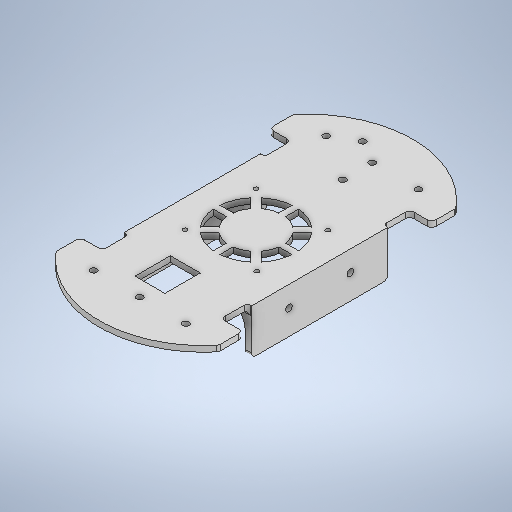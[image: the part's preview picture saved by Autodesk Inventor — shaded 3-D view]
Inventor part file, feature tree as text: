
AUTODESK INVENTOR PART (.ipt)
format: ipt  version: 2025.2 (Build 292293000, 293)  size: 749,056 bytes
history: native  units: mm
features: fillet x34, extrude x14, sketch x14
ambient origin geometry x8: Origin, YZ Plane, XZ Plane, XY Plane, X Axis, Y Axis, Z Axis, Center Point
bodies: Solid1 (feature_tree)
feature tree (62):
  extrude  "Extrusion1"  Depth=11.0mm
  fillet  "Face Fillet1"
  fillet  "Face Fillet2"
  fillet  "Face Fillet3"
  fillet  "Face Fillet4"
  fillet  "Face Fillet5"
  fillet  "Face Fillet6"
  fillet  "Face Fillet7"
  fillet  "Face Fillet8"
  fillet  "Face Fillet9"
  fillet  "Face Fillet10"
  fillet  "Face Fillet11"
  fillet  "Face Fillet12"
  extrude  "Extrusion3"  Depth=17.5mm
  sketch  "Sketch8"  dims[d23=2.0mm d24=2.0mm]
  sketch  "Sketch9"  dims[d25=2.0mm d26=2.0mm]
  extrude  "Extrusion4"  Depth=74.0mm
  sketch  "Sketch5"  dims[d16=27.0mm d17=2.6mm d18=0.0mm]
  sketch  "Sketch6"  dims[d19=2.0mm d20=2.0mm]
  sketch  "Sketch7"  dims[d21=2.0mm d22=2.0mm]
  extrude  "Extrusion11"  Depth=27.0mm
  extrude  "Extrusion12"  Depth=2.6mm TaperAngle=0.0deg
  extrude  "Extrusion13"  Depth=2.0mm
  extrude  "Extrusion14"  Depth=2.0mm
  extrude  "Extrusion15"  Depth=2.0mm
  fillet  "Face Fillet17"
  fillet  "Face Fillet18"
  fillet  "Face Fillet19"
  fillet  "Face Fillet20"
  extrude  "Extrusion16"  Depth=2.0mm
  sketch  "Sketch15"  dims[d27=2.0mm d39=0.0mm d40=40.0mm]
  extrude  "Extrusion17"  Depth=40.0mm TaperAngle=0.0deg
  sketch  "Sketch17"  dims[d48=2.0mm d49=2.0mm]
  extrude  "Extrusion18"  Depth=8.999549mm
  extrude  "Extrusion19"  Depth=2.0mm
  extrude  "Extrusion20"  Depth=12.0mm
  fillet  "Face Fillet24"
  fillet  "Fillet5"  Radius=19.0mm
  fillet  "Fillet6"  Radius=24.0mm
  fillet  "Fillet8"  Radius=1.3mm
  fillet  "Face Fillet25"
  fillet  "Fillet9"  Radius=1.3mm
  fillet  "Face Fillet26"
  fillet  "Face Fillet27"
  fillet  "Face Fillet28"
  fillet  "Face Fillet29"
  fillet  "Fillet10"  Radius=1.3mm
  fillet  "Fillet11"  Radius=1.3mm
  fillet  "Fillet12"  Radius=40.0mm
  fillet  "Fillet13"  Radius=1.5mm
  fillet  "Fillet14"  Radius=40.0mm
  fillet  "Fillet15"  Radius=1.5mm
  fillet  "Fillet16"  Radius=3.0mm
  fillet  "Fillet17"  Radius=21.0mm
  sketch  "Sketch1"  dims[d1=86.0mm d2=11.0mm]
  sketch  "Sketch3"  dims[d5=17.5mm d11=74.0mm]
  sketch  "Sketch4"  dims[d12=74.0mm d15=27.0mm]
  sketch  "Sketch16"  dims[d46=9.0mm d47=8.999549mm]
  sketch  "Sketch18"  dims[d50=2.0mm d51=12.0mm d52=19.0mm d53=24.0mm d54=1.3mm d55=1.3mm d56=1.3mm d57=1.3mm d58=40.0mm d59=0.0mm d60=1.5mm d61=40.0mm d62=0.0mm d63=1.5mm d64=3.0mm d65=21.0mm]
  sketch  "Sketch19"  dims[d66=21.0mm d67=10.0mm d68=2.9mm d69=2.9mm d70=2.9mm d71=10.0mm d72=3.0mm d73=3.0mm d74=3.0mm d75=18.0mm d76=18.0mm d77=3.0mm d78=26.9mm d79=70.0mm d80=26.9mm d81=10.5mm d82=10.5mm d83=2.0mm d84=2.0mm d85=2.0mm d86=2.0mm d87=18.0mm d88=82.0mm d89=31.0mm d90=31.0mm d91=31.0mm d92=18.0mm d118=10.0mm d119=0.0mm d120=10.0mm d121=0.0mm d122=10.0mm d123=0.0mm d124=16.0mm d125=18.0mm d126=20.6mm d127=2.0mm d128=1.0mm d129=0.0mm d130=0.0mm d131=2.0mm d132=1.0mm d133=0.0mm d134=0.0mm d135=2.0mm d136=2.0mm d137=2.0mm d138=2.0mm d139=14.0mm d140=14.0mm d141=9.3mm d142=3.0mm d143=3.0mm d144=3.0mm d145=3.0mm d146=40.0mm d147=5.0mm d148=0.0mm d149=0.0mm d150=40.0mm d151=0.0mm d152=20.0mm d153=0.0mm d154=1.5mm d155=9.0mm d156=4.0mm d157=9.0mm d158=4.0mm d159=1.5mm d160=9.0mm d161=4.0mm d162=9.0mm d163=4.0mm d164=10.0mm d165=0.0mm d166=10.0mm d167=0.0mm d168=45.0mm d169=0.0mm d176=5.0mm d180=5.0mm d182=3.0mm d183=6.67mm d184=6.67mm d186=6.67mm d187=3.0mm d188=6.67mm d189=1.4mm d190=1.4mm d191=1.4mm d192=1.4mm d193=1.4mm d194=1.4mm d195=1.4mm d196=1.4mm d197=1.4mm d198=1.4mm d199=1.4mm d200=1.4mm d201=3.333333mm d112=0.5mm d113=0.872665mm d114=0.5mm d115=0.872665mm d170=0.0mm d171=0.0mm]
  sketch  "Sketch2"  dims[d3=11.0mm d4=17.5mm]
  extrude  "Extrusion2"  Depth=10.0mm
